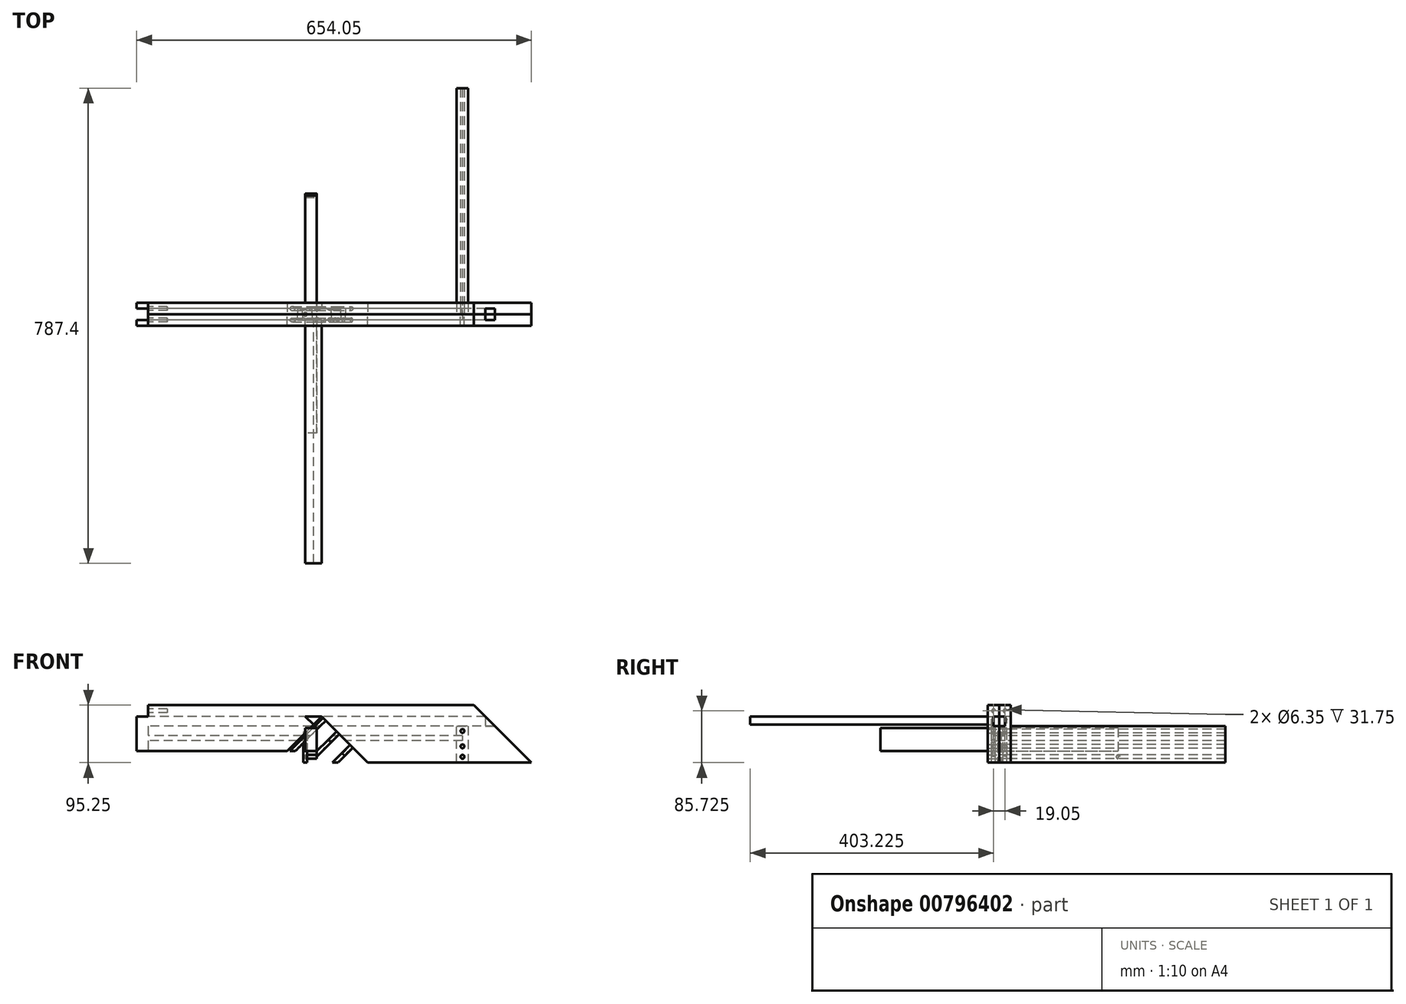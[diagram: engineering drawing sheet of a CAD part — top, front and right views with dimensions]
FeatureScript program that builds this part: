
annotation { "Feature Type Name" : "Feature", "Feature Type Description" : "" }
export const myFeature = defineFeature(function(context is Context, id is Id, definition is map)
    precondition{}
    {
        {
            var Q0;
            Q0=qCreatedBy(makeId("Front.planeOp"),FACE);
            var sketch = newSketch(context, id + "F0", { "sketchPlane" : qUnion([Q0])});
            skLineSegment(sketch, "E0", {"start": v(-260.35, 0) * mm, "end": v(374.65, 0) * mm});
            skLineSegment(sketch, "E1", {"start": v(374.65, 0) * mm, "end": v(279.4, 95.25) * mm});
            skLineSegment(sketch, "E2", {"start": v(-279.4, 19.05) * mm, "end": v(-279.4, 76.2) * mm});
            skLineSegment(sketch, "E3", {"start": v(-260.35, 95.25) * mm, "end": v(279.4, 95.25) * mm});
            skLineSegment(sketch, "E4", {"start": v(-260.35, 0) * mm, "end": v(-260.35, 19.05) * mm});
            skLineSegment(sketch, "E5", {"start": v(-260.35, 19.05) * mm, "end": v(-279.4, 19.05) * mm});
            skLineSegment(sketch, "E6", {"start": v(-260.35, 95.25) * mm, "end": v(-260.35, 76.2) * mm});
            skLineSegment(sketch, "E7", {"start": v(-260.35, 76.2) * mm, "end": v(-279.4, 76.2) * mm});
            skSolve(sketch);
        }
        {
            var Q0;
            Q0=makeQuery(id+"F0.imprint","IMPRINT",FACE,{"disambiguationData":[TD([[makeQuery(id+"F0.imprint","IMPRINT",EDGE,{"derivedFrom":sQuery(id+"F0.wireOp",EDGE,"E0")}),1.0]])]});
            extrude(context, id + "F1", {"entities" : qUnion([Q0]), "depth" : 19.05 * mm, "offsetDistance" : 25.4 * mm});
        }
        {
            var Q0;
            Q0=makeQuery(id+"F1.opExtrude","SWEPT_FACE",FACE,{"disambiguationData":[OSD([sQuery(id+"F0.wireOp",EDGE,"E7")])]});
            var sketch = newSketch(context, id + "F2", { "sketchPlane" : qUnion([Q0])});
            skLineSegment(sketch, "E8", {"start": v(-279.4, -9.53) * mm, "end": v(-260.35, -9.53) * mm});
            skSolve(sketch);
        }
        {
            var Q0;
            {var subQ0=sQuery(id+"F2.wireOp",EDGE,"E8");Q0=makeQuery(id+"F2.imprint","IMPRINT",FACE,{"disambiguationData":[TD([[makeQuery(id+"F2.imprint","IMPRINT",EDGE,{"derivedFrom":subQ0}),1.0]])]});}
            extrude(context, id + "F3", {"entities" : qUnion([Q0]), "operationType" : NewBodyOperationType.REMOVE, "endBound" : BoundingType.THROUGH_ALL, "oppositeDirection" : true, "depth" : 25.4 * mm, "offsetDistance" : 25.4 * mm});
        }
        {
            var Q0;
            {var subQ0=sQuery(id+"F0.wireOp",EDGE,"E6");Q0=makeQuery(id+"F3.boolean.opBoolean","MERGE",FACE,{"derivedFrom":[makeQuery(id+"F1.opExtrude","SWEPT_FACE",FACE,{"disambiguationData":[OSD([sQuery(id+"F0.wireOp",EDGE,"E4")])]}),makeQuery(id+"F1.opExtrude","SWEPT_FACE",FACE,{"disambiguationData":[OSD([subQ0])]}),makeQuery(id+"F3.opExtrude","SWEPT_FACE",FACE,{"disambiguationData":[OSD([subQ0,sQuery(id+"F0.wireOp",EDGE,"E7")])]})]});}
            var sketch = newSketch(context, id + "F4", { "sketchPlane" : qUnion([Q0])});
            skLineSegment(sketch, "E9", {"start": v(0, 76.2) * mm, "end": v(9.53, 76.2) * mm});
            skLineSegment(sketch, "E10", {"start": v(9.53, 76.2) * mm, "end": v(9.53, 60.33) * mm});
            skLineSegment(sketch, "E11", {"start": v(9.53, 60.33) * mm, "end": v(0, 60.33) * mm});
            skLineSegment(sketch, "E12", {"start": v(0, 44.45) * mm, "end": v(9.53, 44.45) * mm});
            skLineSegment(sketch, "E13", {"start": v(9.53, 44.45) * mm, "end": v(9.53, 36.51) * mm});
            skLineSegment(sketch, "E14", {"start": v(9.53, 36.51) * mm, "end": v(0, 36.51) * mm});
            skSolve(sketch);
        }
        {
            var Q0;
            {var subQ0=sQuery(id+"F4.wireOp",EDGE,"E12");Q0=makeQuery(id+"F4.imprint","IMPRINT",FACE,{"disambiguationData":[TD([[makeQuery(id+"F4.imprint","IMPRINT",EDGE,{"derivedFrom":subQ0}),-1.0]])]});}
            extrude(context, id + "F5", {"entities" : qUnion([Q0]), "operationType" : NewBodyOperationType.REMOVE, "oppositeDirection" : true, "depth" : 520.7 * mm, "offsetDistance" : 25.4 * mm});
        }
        {
            var Q0;
            Q0=makeQuery(id+"F1.opExtrude","CAP_FACE",FACE,{"disambiguationData":[OSD([sQuery(id+"F0.wireOp",EDGE,"E0"),sQuery(id+"F0.wireOp",EDGE,"E1"),sQuery(id+"F0.wireOp",EDGE,"E2"),sQuery(id+"F0.wireOp",EDGE,"E3"),sQuery(id+"F0.wireOp",EDGE,"E4"),sQuery(id+"F0.wireOp",EDGE,"E5"),sQuery(id+"F0.wireOp",EDGE,"E6"),sQuery(id+"F0.wireOp",EDGE,"E7")])],"isStart":true});
            var sketch = newSketch(context, id + "F6", { "sketchPlane" : qUnion([Q0])});
            skLineSegment(sketch, "E15", {"start": v(-269.88, 60.33) * mm, "end": v(-269.88, 0) * mm});
            skLineSegment(sketch, "E16", {"start": v(-269.88, 0) * mm, "end": v(-250.83, 0) * mm});
            skLineSegment(sketch, "E17", {"start": v(-250.83, 0) * mm, "end": v(-250.83, 36.51) * mm});
            skLineSegment(sketch, "E18", {"start": v(-250.83, 36.51) * mm, "end": v(-260.35, 36.51) * mm});
            skLineSegment(sketch, "E19", {"start": v(-260.35, 36.51) * mm, "end": v(-260.35, 44.45) * mm});
            skLineSegment(sketch, "E20", {"start": v(-260.35, 44.45) * mm, "end": v(-250.82, 44.45) * mm});
            skLineSegment(sketch, "E21", {"start": v(-250.82, 44.45) * mm, "end": v(-250.82, 60.33) * mm});
            skLineSegment(sketch, "E22", {"start": v(-250.82, 60.33) * mm, "end": v(-269.88, 60.33) * mm});
            skSolve(sketch);
        }
        {
            var Q0;
            Q0=makeQuery(id+"F1.opExtrude","CAP_FACE",FACE,{"disambiguationData":[OSD([sQuery(id+"F0.wireOp",EDGE,"E0"),sQuery(id+"F0.wireOp",EDGE,"E1"),sQuery(id+"F0.wireOp",EDGE,"E2"),sQuery(id+"F0.wireOp",EDGE,"E3"),sQuery(id+"F0.wireOp",EDGE,"E4"),sQuery(id+"F0.wireOp",EDGE,"E5"),sQuery(id+"F0.wireOp",EDGE,"E6"),sQuery(id+"F0.wireOp",EDGE,"E7")])],"isStart":true});
            var sketch = newSketch(context, id + "F7", { "sketchPlane" : qUnion([Q0])});
            skLineSegment(sketch, "E23", {"start": v(-260.35, 44.45) * mm, "end": v(-260.35, 44.45) * mm});
            skCircle(sketch, "E24", {"center": v(-260.35, 52.39) * mm, "radius": 3.18 * mm});
            skCircle(sketch, "E25", {"center": v(-260.35, 26.99) * mm, "radius": 3.18 * mm});
            skCircle(sketch, "E26", {"center": v(-260.35, 9.53) * mm, "radius": 3.18 * mm});
            skSolve(sketch);
        }
        {
            var Q0;
            Q0=qCreatedBy(makeId("Front.planeOp"),FACE);
            var sketch = newSketch(context, id + "F8", { "sketchPlane" : qUnion([Q0])});
            skLineSegment(sketch, "E27", {"start": v(0, 76.2) * mm, "end": v(76.2, 0) * mm});
            skLineSegment(sketch, "E28.0", {"start": v(26.94, 76.2) * mm, "end": v(103.14, 0) * mm});
            skLineSegment(sketch, "E29", {"start": v(0, 76.2) * mm, "end": v(26.94, 76.2) * mm});
            skLineSegment(sketch, "E30", {"start": v(76.2, 0) * mm, "end": v(103.14, 0) * mm});
            skSolve(sketch);
        }
        {
            var Q0;
            Q0=makeQuery(id+"F8.imprint","IMPRINT",FACE,{"disambiguationData":[TD([[makeQuery(id+"F8.imprint","IMPRINT",EDGE,{"derivedFrom":sQuery(id+"F8.wireOp",EDGE,"E27")}),1.0]])]});
            extrude(context, id + "F9", {"entities" : qUnion([Q0]), "depth" : 412.75 * mm, "offsetDistance" : 25.4 * mm});
        }
        {
            var Q0;
            Q0=makeQuery(id+"F9.opExtrude","SWEPT_FACE",FACE,{"disambiguationData":[OSD([sQuery(id+"F8.wireOp",EDGE,"E28.0")])]});
            var sketch = newSketch(context, id + "F10", { "sketchPlane" : qUnion([Q0])});
            skCircle(sketch, "E31", {"center": v(-403.23, 28.48) * mm, "radius": 3.18 * mm});
            skCircle(sketch, "E32", {"center": v(-403.23, -3.27) * mm, "radius": 3.18 * mm});
            skCircle(sketch, "E33", {"center": v(-403.23, -35.02) * mm, "radius": 3.18 * mm});
            skLineSegment(sketch, "E34", {"start": v(-206.38, 34.83) * mm, "end": v(-206.38, -72.93) * mm, "construction": true});
            skCircle(sketch, "E35.MirrorC", {"center": v(-9.53, 28.48) * mm, "radius": 3.18 * mm});
            skCircle(sketch, "E36.MirrorC", {"center": v(-9.53, -3.27) * mm, "radius": 3.18 * mm});
            skCircle(sketch, "E37.MirrorC", {"center": v(-9.53, -35.02) * mm, "radius": 3.18 * mm});
            skSolve(sketch);
        }
        {
            var Q0;
            Q0=makeQuery(id+"F10.imprint","IMPRINT",FACE,{"disambiguationData":[TD([[makeQuery(id+"F10.imprint","IMPRINT",EDGE,{"derivedFrom":sQuery(id+"F10.wireOp",EDGE,"E31")}),1.0]])]});
            var Q1;
            Q1=makeQuery(id+"F10.imprint","IMPRINT",FACE,{"disambiguationData":[TD([[makeQuery(id+"F10.imprint","IMPRINT",EDGE,{"derivedFrom":sQuery(id+"F10.wireOp",EDGE,"E32")}),1.0]])]});
            var Q2;
            Q2=makeQuery(id+"F10.imprint","IMPRINT",FACE,{"disambiguationData":[TD([[makeQuery(id+"F10.imprint","IMPRINT",EDGE,{"derivedFrom":sQuery(id+"F10.wireOp",EDGE,"E33")}),1.0]])]});
            var Q3;
            Q3=makeQuery(id+"F10.imprint","IMPRINT",FACE,{"disambiguationData":[TD([[makeQuery(id+"F10.imprint","IMPRINT",EDGE,{"derivedFrom":sQuery(id+"F10.wireOp",EDGE,"E35.MirrorC")}),-1.0]])]});
            var Q4;
            Q4=makeQuery(id+"F10.imprint","IMPRINT",FACE,{"disambiguationData":[TD([[makeQuery(id+"F10.imprint","IMPRINT",EDGE,{"derivedFrom":sQuery(id+"F10.wireOp",EDGE,"E36.MirrorC")}),-1.0]])]});
            var Q5;
            Q5=makeQuery(id+"F10.imprint","IMPRINT",FACE,{"disambiguationData":[TD([[makeQuery(id+"F10.imprint","IMPRINT",EDGE,{"derivedFrom":sQuery(id+"F10.wireOp",EDGE,"E37.MirrorC")}),-1.0]])]});
            extrude(context, id + "F11", {"entities" : qUnion([Q0, Q1, Q2, Q3, Q4, Q5]), "operationType" : NewBodyOperationType.REMOVE, "endBound" : BoundingType.THROUGH_ALL, "oppositeDirection" : true, "depth" : 25.4 * mm, "offsetDistance" : 25.4 * mm});
        }
        {
            var Q0;
            Q0=qCreatedBy(makeId("Right.planeOp"),FACE);
            var sketch = newSketch(context, id + "F12", { "sketchPlane" : qUnion([Q0])});
            skLineSegment(sketch, "E38.bottom", {"start": v(-206.38, 0) * mm, "end": v(206.38, 0) * mm});
            skLineSegment(sketch, "E38.top", {"start": v(-206.38, 19.05) * mm, "end": v(206.38, 19.05) * mm});
            skLineSegment(sketch, "E38.left", {"start": v(-206.38, 0) * mm, "end": v(-206.38, 19.05) * mm});
            skLineSegment(sketch, "E38.right", {"start": v(206.38, 0) * mm, "end": v(206.38, 19.05) * mm});
            skSolve(sketch);
        }
        {
            var Q0;
            Q0=makeQuery(id+"F12.imprint","IMPRINT",FACE,{"disambiguationData":[TD([[makeQuery(id+"F12.imprint","IMPRINT",EDGE,{"derivedFrom":sQuery(id+"F12.wireOp",EDGE,"E38.bottom")}),1.0]])]});
            extrude(context, id + "F13", {"entities" : qUnion([Q0]), "depth" : 19.05 * mm, "offsetDistance" : 25.4 * mm});
        }
        {
            var Q0;
            Q0=qCreatedBy(makeId("Top.planeOp"),FACE);
            var sketch = newSketch(context, id + "F14", { "sketchPlane" : qUnion([Q0])});
            skLineSegment(sketch, "E39.bottom", {"start": v(0, 196.85) * mm, "end": v(19.05, 196.85) * mm});
            skLineSegment(sketch, "E39.top", {"start": v(0, -196.85) * mm, "end": v(19.05, -196.85) * mm});
            skLineSegment(sketch, "E39.left", {"start": v(0, 196.85) * mm, "end": v(0, -196.85) * mm});
            skLineSegment(sketch, "E39.right", {"start": v(19.05, 196.85) * mm, "end": v(19.05, -196.85) * mm});
            skSolve(sketch);
        }
        {
            var Q0;
            Q0=makeQuery(id+"F14.imprint","IMPRINT",FACE,{"disambiguationData":[TD([[makeQuery(id+"F14.imprint","IMPRINT",EDGE,{"derivedFrom":sQuery(id+"F14.wireOp",EDGE,"E39.bottom")}),-1.0]])]});
            extrude(context, id + "F15", {"entities" : qUnion([Q0]), "depth" : 57.15 * mm, "offsetDistance" : 25.4 * mm});
        }
        {
            var Q0;
            {var subQ0=sQuery(id+"F0.wireOp",EDGE,"E7");var subQ1=sQuery(id+"F0.wireOp",EDGE,"E3");var subQ2=sQuery(id+"F0.wireOp",EDGE,"E6");var subQ4=sQuery(id+"F0.wireOp",EDGE,"E4");Q0=makeQuery(id+"F5.boolean.opBoolean","SPLIT",FACE,{"disambiguationData":[TD([makeQuery(id+"F1.opExtrude","SWEPT_FACE",FACE,{"disambiguationData":[OSD([subQ1])]})])],"derivedFrom":makeQuery(id+"F3.boolean.opBoolean","MERGE",FACE,{"derivedFrom":[makeQuery(id+"F1.opExtrude","SWEPT_FACE",FACE,{"disambiguationData":[OSD([subQ4])]}),makeQuery(id+"F1.opExtrude","SWEPT_FACE",FACE,{"disambiguationData":[OSD([subQ2])]}),makeQuery(id+"F3.opExtrude","SWEPT_FACE",FACE,{"disambiguationData":[OSD([subQ2,subQ0])]})]})});}
            var sketch = newSketch(context, id + "F16", { "sketchPlane" : qUnion([Q0])});
            skCircle(sketch, "E40", {"center": v(9.53, 85.73) * mm, "radius": 3.18 * mm});
            skPoint(sketch, "E40.centerSnap0", {"position": v(19.05, 85.73) * mm});
            skPoint(sketch, "E40.centerSnap1", {"position": v(9.53, 95.25) * mm});
            skSolve(sketch);
        }
        {
            var Q0;
            Q0=makeQuery(id+"F16.imprint","IMPRINT",FACE,{"disambiguationData":[TD([[makeQuery(id+"F16.imprint","IMPRINT",EDGE,{"derivedFrom":sQuery(id+"F16.wireOp",EDGE,"E40")}),1.0]])]});
            extrude(context, id + "F17", {"entities" : qUnion([Q0]), "operationType" : NewBodyOperationType.REMOVE, "oppositeDirection" : true, "depth" : 31.75 * mm, "offsetDistance" : 25.4 * mm});
        }
        {
            var Q0;
            {var subQ1=sQuery(id+"F0.wireOp",EDGE,"E7");var subQ2=sQuery(id+"F0.wireOp",EDGE,"E6");var subQ3=sQuery(id+"F0.wireOp",EDGE,"E4");var subQ7=sQuery(id+"F0.wireOp",EDGE,"E0");Q0=makeQuery(id+"F5.boolean.opBoolean","SPLIT",FACE,{"disambiguationData":[TD([makeQuery(id+"F1.opExtrude","SWEPT_FACE",FACE,{"disambiguationData":[OSD([subQ7])]})])],"derivedFrom":makeQuery(id+"F3.boolean.opBoolean","MERGE",FACE,{"derivedFrom":[makeQuery(id+"F1.opExtrude","SWEPT_FACE",FACE,{"disambiguationData":[OSD([subQ3])]}),makeQuery(id+"F1.opExtrude","SWEPT_FACE",FACE,{"disambiguationData":[OSD([subQ2])]}),makeQuery(id+"F3.opExtrude","SWEPT_FACE",FACE,{"disambiguationData":[OSD([subQ2,subQ1])]})]})});}
            var sketch = newSketch(context, id + "F18", { "sketchPlane" : qUnion([Q0])});
            skCircle(sketch, "E41", {"center": v(9.53, 9.53) * mm, "radius": 3.18 * mm});
            skPoint(sketch, "E41.centerSnap0", {"position": v(19.05, 9.53) * mm});
            skPoint(sketch, "E41.centerSnap1", {"position": v(9.53, 0) * mm});
            skSolve(sketch);
        }
        {
            var Q0;
            Q0=makeQuery(id+"F18.imprint","IMPRINT",FACE,{"disambiguationData":[TD([[makeQuery(id+"F18.imprint","IMPRINT",EDGE,{"derivedFrom":sQuery(id+"F18.wireOp",EDGE,"E41")}),1.0]])]});
            extrude(context, id + "F19", {"entities" : qUnion([Q0]), "operationType" : NewBodyOperationType.REMOVE, "oppositeDirection" : true, "depth" : 31.75 * mm, "offsetDistance" : 25.4 * mm});
        }
        {
            var Q0;
            Q0=qCreatedBy(makeId("Top.planeOp"),FACE);
            var sketch = newSketch(context, id + "F20", { "sketchPlane" : qUnion([Q0])});
            skCircle(sketch, "E42", {"center": v(0, 0) * mm, "radius": 3.18 * mm});
            skSolve(sketch);
        }
        {
            var Q0;
            Q0=makeQuery(id+"F20.imprint","IMPRINT",FACE,{"disambiguationData":[TD([[makeQuery(id+"F20.imprint","IMPRINT",EDGE,{"derivedFrom":sQuery(id+"F20.wireOp",EDGE,"E42")}),1.0]])]});
            extrude(context, id + "F21", {"entities" : qUnion([Q0]), "depth" : 50.8 * mm, "offsetDistance" : 25.4 * mm});
        }
        {
            var Q0;
            Q0=makeQuery(id+"F13.opExtrude","CAP_FACE",FACE,{"disambiguationData":[OSD([sQuery(id+"F12.wireOp",EDGE,"E38.bottom"),sQuery(id+"F12.wireOp",EDGE,"E38.top"),sQuery(id+"F12.wireOp",EDGE,"E38.left"),sQuery(id+"F12.wireOp",EDGE,"E38.right")])],"isStart":false});
            var sketch = newSketch(context, id + "F22", { "sketchPlane" : qUnion([Q0])});
            skCircle(sketch, "E43", {"center": v(-196.85, 9.53) * mm, "radius": 3.18 * mm});
            skPoint(sketch, "E43.centerSnap0", {"position": v(-206.38, 9.53) * mm});
            skCircle(sketch, "E44.MirrorC", {"center": v(196.85, 9.53) * mm, "radius": 3.18 * mm});
            skSolve(sketch);
        }
        {
            var Q0;
            Q0=makeQuery(id+"F22.imprint","IMPRINT",FACE,{"disambiguationData":[TD([[makeQuery(id+"F22.imprint","IMPRINT",EDGE,{"derivedFrom":sQuery(id+"F22.wireOp",EDGE,"E43")}),1.0]])]});
            var Q1;
            Q1=makeQuery(id+"F22.imprint","IMPRINT",FACE,{"disambiguationData":[TD([[makeQuery(id+"F22.imprint","IMPRINT",EDGE,{"derivedFrom":sQuery(id+"F22.wireOp",EDGE,"E44.MirrorC")}),-1.0]])]});
            extrude(context, id + "F23", {"entities" : qUnion([Q0, Q1]), "operationType" : NewBodyOperationType.REMOVE, "endBound" : BoundingType.THROUGH_ALL, "oppositeDirection" : true, "depth" : 25.4 * mm, "offsetDistance" : 25.4 * mm});
        }
        {
            var Q0;
            {var subQ0=sQuery(id+"F6.wireOp",EDGE,"E15");Q0=makeQuery(id+"F6.imprint","IMPRINT",FACE,{"disambiguationData":[TD([[makeQuery(id+"F6.imprint","IMPRINT",EDGE,{"derivedFrom":subQ0}),1.0]])]});}
            extrude(context, id + "F24", {"entities" : qUnion([Q0]), "depth" : 374.65 * mm, "offsetDistance" : 25.4 * mm});
        }
        {
            var Q0;
            Q0=makeQuery(id+"F7.imprint","IMPRINT",FACE,{"disambiguationData":[TD([[makeQuery(id+"F7.imprint","IMPRINT",EDGE,{"derivedFrom":sQuery(id+"F7.wireOp",EDGE,"E24")}),1.0]])]});
            var Q1;
            Q1=makeQuery(id+"F7.imprint","IMPRINT",FACE,{"disambiguationData":[TD([[makeQuery(id+"F7.imprint","IMPRINT",EDGE,{"derivedFrom":sQuery(id+"F7.wireOp",EDGE,"E25")}),1.0]])]});
            var Q2;
            Q2=makeQuery(id+"F7.imprint","IMPRINT",FACE,{"disambiguationData":[TD([[makeQuery(id+"F7.imprint","IMPRINT",EDGE,{"derivedFrom":sQuery(id+"F7.wireOp",EDGE,"E26")}),1.0]])]});
            extrude(context, id + "F25", {"entities" : qUnion([Q0, Q1, Q2]), "operationType" : NewBodyOperationType.REMOVE, "endBound" : BoundingType.THROUGH_ALL, "depth" : 25.4 * mm, "offsetDistance" : 25.4 * mm});
        }
        {
            var Q0;
            {var subQ0=sQuery(id+"F4.wireOp",EDGE,"E9");Q0=makeQuery(id+"F4.imprint","IMPRINT",FACE,{"disambiguationData":[TD([[makeQuery(id+"F4.imprint","IMPRINT",EDGE,{"derivedFrom":subQ0}),-1.0]])]});}
            extrude(context, id + "F26", {"entities" : qUnion([Q0]), "operationType" : NewBodyOperationType.REMOVE, "endBound" : BoundingType.THROUGH_ALL, "oppositeDirection" : true, "depth" : 25.4 * mm, "offsetDistance" : 25.4 * mm});
        }
        {
            var Q0;
            Q0=makeQuery(id+"F26.boolean.opBoolean","MERGE",FACE,{"derivedFrom":[makeQuery(id+"F5.boolean.opBoolean","MERGE",FACE,{"derivedFrom":[makeQuery(id+"F3.boolean.opBoolean","COPY",FACE,{"derivedFrom":makeQuery(id+"F3.opExtrude","SWEPT_FACE",FACE,{"disambiguationData":[OSD([sQuery(id+"F2.wireOp",EDGE,"E8")])]})}),makeQuery(id+"F5.opExtrude","SWEPT_FACE",FACE,{"disambiguationData":[OSD([sQuery(id+"F4.wireOp",EDGE,"E13")])]})]}),makeQuery(id+"F26.opExtrude","SWEPT_FACE",FACE,{"disambiguationData":[OSD([sQuery(id+"F4.wireOp",EDGE,"E10")])]})]});
            var sketch = newSketch(context, id + "F27", { "sketchPlane" : qUnion([Q0])});
            skLineSegment(sketch, "E45", {"start": v(-298.45, 76.2) * mm, "end": v(-298.45, 60.33) * mm});
            skLineSegment(sketch, "E46", {"start": v(-298.45, 60.33) * mm, "end": v(-314.32, 60.33) * mm});
            skLineSegment(sketch, "E47", {"start": v(-314.32, 60.33) * mm, "end": v(-298.45, 76.2) * mm});
            skSolve(sketch);
        }
        {
            var Q0;
            Q0=makeQuery(id+"F27.imprint","IMPRINT",FACE,{"disambiguationData":[TD([[makeQuery(id+"F27.imprint","IMPRINT",EDGE,{"derivedFrom":sQuery(id+"F27.wireOp",EDGE,"E45")}),-1.0]])]});
            extrude(context, id + "F28", {"entities" : qUnion([Q0]), "depth" : 9.52 * mm, "offsetDistance" : 25.4 * mm});
        }
        {
            var Q0;
            Q0=makeQuery(id+"F7.imprint","IMPRINT",FACE,{"disambiguationData":[TD([[makeQuery(id+"F7.imprint","IMPRINT",EDGE,{"derivedFrom":sQuery(id+"F7.wireOp",EDGE,"E24")}),1.0]])]});
            var Q1;
            Q1=makeQuery(id+"F7.imprint","IMPRINT",FACE,{"disambiguationData":[TD([[makeQuery(id+"F7.imprint","IMPRINT",EDGE,{"derivedFrom":sQuery(id+"F7.wireOp",EDGE,"E25")}),1.0]])]});
            var Q2;
            Q2=makeQuery(id+"F7.imprint","IMPRINT",FACE,{"disambiguationData":[TD([[makeQuery(id+"F7.imprint","IMPRINT",EDGE,{"derivedFrom":sQuery(id+"F7.wireOp",EDGE,"E26")}),1.0]])]});
            extrude(context, id + "F29", {"entities" : qUnion([Q0, Q1, Q2]), "operationType" : NewBodyOperationType.REMOVE, "endBound" : BoundingType.THROUGH_ALL, "oppositeDirection" : true, "depth" : 25.4 * mm, "offsetDistance" : 25.4 * mm});
        }
        {
            var Q0;
            Q0=makeQuery(id+"F1.opExtrude","SWEPT_BODY",BODY,{"disambiguationData":[OSD([sQuery(id+"F0.wireOp",EDGE,"E0"),sQuery(id+"F0.wireOp",EDGE,"E1"),sQuery(id+"F0.wireOp",EDGE,"E2"),sQuery(id+"F0.wireOp",EDGE,"E3"),sQuery(id+"F0.wireOp",EDGE,"E4"),sQuery(id+"F0.wireOp",EDGE,"E5"),sQuery(id+"F0.wireOp",EDGE,"E6"),sQuery(id+"F0.wireOp",EDGE,"E7")])]});
            var Q1;
            Q1=qCreatedBy(makeId("Front.planeOp"),FACE);
            mirror(context, id + "F30", {"entities" : qUnion([Q0]), "mirrorPlane" : qUnion([Q1])});
        }
        {
            var Q0;
            Q0=makeQuery(id+"F15.opExtrude","SWEPT_FACE",FACE,{"disambiguationData":[OSD([sQuery(id+"F14.wireOp",EDGE,"E39.top")])]});
            var sketch = newSketch(context, id + "F31", { "sketchPlane" : qUnion([Q0])});
            skLineSegment(sketch, "E48", {"start": v(0, 0) * mm, "end": v(19.05, 0) * mm});
            skLineSegment(sketch, "E49", {"start": v(19.05, 0) * mm, "end": v(19.05, 3.27) * mm});
            skArc(sketch, "E50", {"start": v(0, 0) * mm, "mid": v(9.66, 0.82) * mm, "end": v(19.05, 3.27) * mm});
            skSolve(sketch);
        }
        {
            var Q0;
            Q0=makeQuery(id+"F31.imprint","IMPRINT",FACE,{"disambiguationData":[TD([[makeQuery(id+"F31.imprint","IMPRINT",EDGE,{"derivedFrom":sQuery(id+"F31.wireOp",EDGE,"E48")}),1.0]])]});
            extrude(context, id + "F32", {"entities" : qUnion([Q0]), "operationType" : NewBodyOperationType.REMOVE, "endBound" : BoundingType.THROUGH_ALL, "oppositeDirection" : true, "depth" : 25.4 * mm, "offsetDistance" : 25.4 * mm});
        }
        {
            var Q0;
            Q0=qCreatedBy(makeId("Top.planeOp"),FACE);
            var sketch = newSketch(context, id + "F33", { "sketchPlane" : qUnion([Q0])});
            skCircle(sketch, "E51", {"center": v(0, 0) * mm, "radius": 3.18 * mm});
            skSolve(sketch);
        }
        {
            var Q0;
            Q0=makeQuery(id+"F33.imprint","IMPRINT",FACE,{"disambiguationData":[TD([[makeQuery(id+"F33.imprint","IMPRINT",EDGE,{"derivedFrom":sQuery(id+"F33.wireOp",EDGE,"E51")}),1.0]])]});
            extrude(context, id + "F34", {"entities" : qUnion([Q0]), "depth" : 31.75 * mm, "offsetDistance" : 25.4 * mm});
        }
    });
